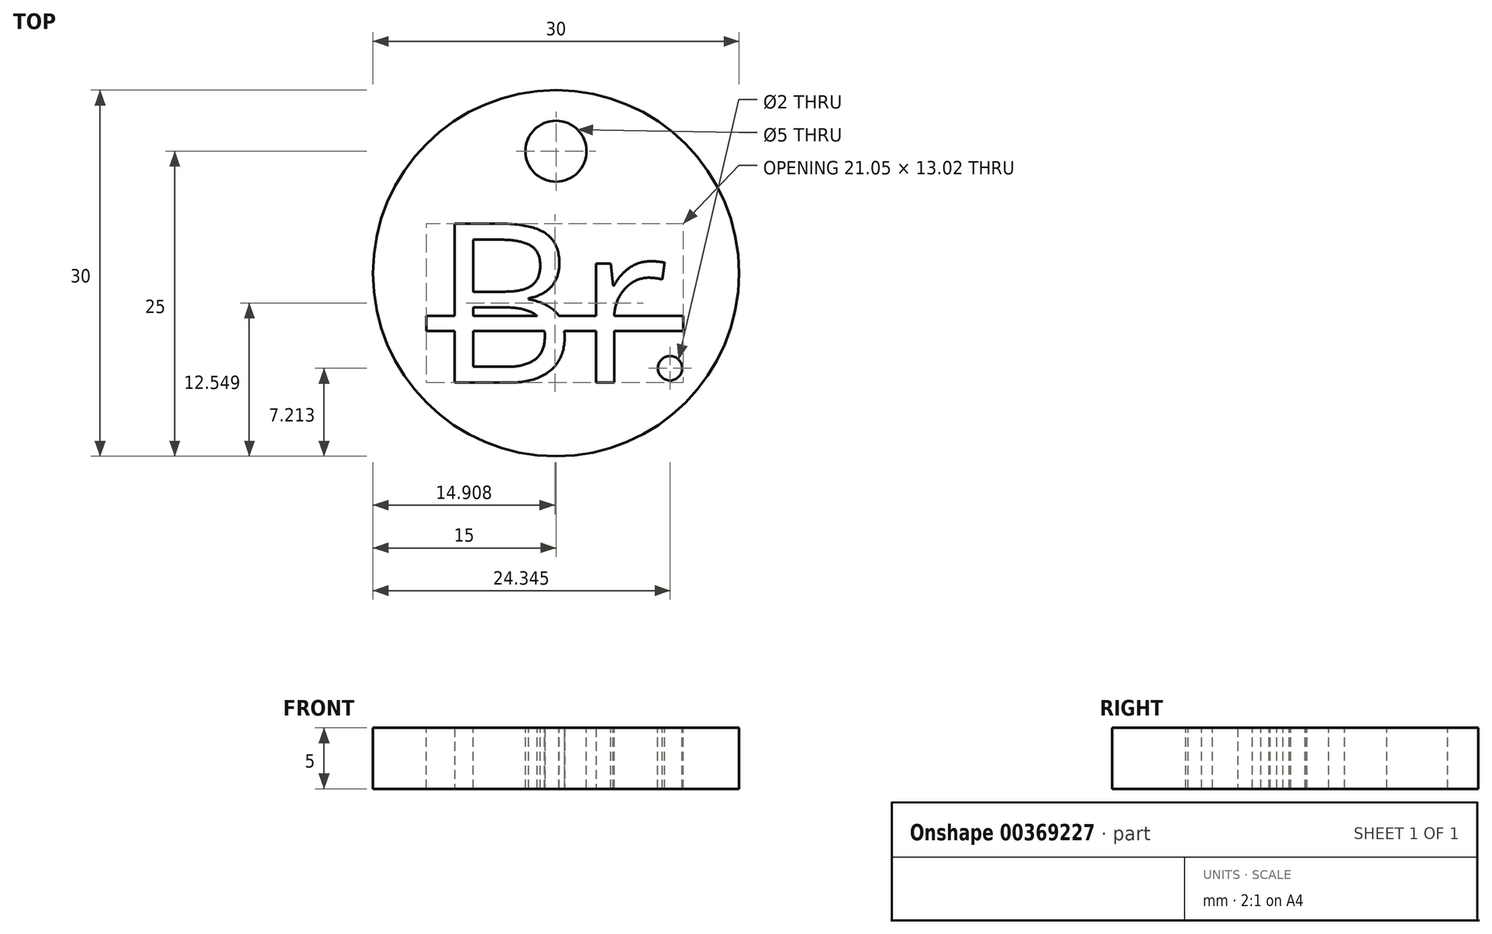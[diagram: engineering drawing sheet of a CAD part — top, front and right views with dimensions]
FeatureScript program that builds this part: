
annotation { "Feature Type Name" : "Feature", "Feature Type Description" : "" }
export const myFeature = defineFeature(function(context is Context, id is Id, definition is map)
    precondition{}
    {
        {
            var Q0;
            Q0=qCreatedBy(makeId("Top.planeOp"),FACE);
            var sketch = newSketch(context, id + "F0", { "sketchPlane" : qUnion([Q0])});
            skCircle(sketch, "E0", {"center": v(0, 0) * mm, "radius": 15 * mm});
            skSolve(sketch);
        }
        {
            var Q0;
            Q0=makeQuery(id+"F0.imprint","IMPRINT",FACE,{"disambiguationData":[TD([[makeQuery(id+"F0.imprint","IMPRINT",EDGE,{"derivedFrom":sQuery(id+"F0.wireOp",EDGE,"E0")}),1.0]])]});
            extrude(context, id + "F1", {"entities" : qUnion([Q0]), "depth" : 5 * mm});
        }
        {
            var Q0;
            Q0=makeQuery(id+"F1.opExtrude","CAP_FACE",FACE,{"disambiguationData":[OSD([sQuery(id+"F0.wireOp",EDGE,"E0")])],"isStart":false});
            var sketch = newSketch(context, id + "F2", { "sketchPlane" : qUnion([Q0])});
            skText(sketch, "E1", { "text": "Br", "fontName": "OpenSans-Regular.ttf"});
            const initialGuessF2  = {"E1": [-0.0101, -0.00896, 1, 0, 0.01313]};
            skSetInitialGuess(sketch, initialGuessF2);
            skSolve(sketch);
        }
        {
            var Q0;
            Q0 = qSketchRegion(id + "F2", true);
            extrude(context, id + "F3", {"entities" : qUnion([Q0]), "operationType" : NewBodyOperationType.REMOVE, "oppositeDirection" : true, "depth" : 25 * mm});
        }
        {
            var Q0;
            {var subQ0=sQuery(id+"F0.wireOp",EDGE,"E0");Q0=makeQuery(id+"F3.boolean.opBoolean","SPLIT",FACE,{"disambiguationData":[TD([makeQuery(id+"F1.opExtrude","SWEPT_FACE",FACE,{"disambiguationData":[OSD([subQ0])]})])],"derivedFrom":makeQuery(id+"F1.opExtrude","CAP_FACE",FACE,{"disambiguationData":[OSD([subQ0])],"isStart":false})});}
            var sketch = newSketch(context, id + "F4", { "sketchPlane" : qUnion([Q0])});
            skLineSegment(sketch, "E2.bottom", {"start": v(-10.61, -3.5) * mm, "end": v(10.43, -3.5) * mm});
            skLineSegment(sketch, "E2.top", {"start": v(-10.61, -4.72) * mm, "end": v(10.43, -4.72) * mm});
            skLineSegment(sketch, "E2.left", {"start": v(-10.61, -3.5) * mm, "end": v(-10.61, -4.72) * mm});
            skLineSegment(sketch, "E2.right", {"start": v(10.43, -3.5) * mm, "end": v(10.43, -4.72) * mm});
            skCircle(sketch, "E3", {"center": v(9.35, -7.79) * mm, "radius": 1 * mm});
            skSolve(sketch);
        }
        {
            var Q0;
            Q0 = qSketchRegion(id + "F4", true);
            extrude(context, id + "F5", {"entities" : qUnion([Q0]), "operationType" : NewBodyOperationType.REMOVE, "endBound" : BoundingType.THROUGH_ALL, "oppositeDirection" : true, "depth" : 25 * mm});
        }
        {
            var Q0;
            {var subQ0=sQuery(id+"F0.wireOp",EDGE,"E0");Q0=makeQuery(id+"F3.boolean.opBoolean","SPLIT",FACE,{"disambiguationData":[TD([makeQuery(id+"F1.opExtrude","SWEPT_FACE",FACE,{"disambiguationData":[OSD([subQ0])]})])],"derivedFrom":makeQuery(id+"F1.opExtrude","CAP_FACE",FACE,{"disambiguationData":[OSD([subQ0])],"isStart":false})});}
            var sketch = newSketch(context, id + "F6", { "sketchPlane" : qUnion([Q0])});
            skCircle(sketch, "E4", {"center": v(0, 10) * mm, "radius": 2.5 * mm});
            skSolve(sketch);
        }
        {
            var Q0;
            Q0 = qSketchRegion(id + "F6", true);
            extrude(context, id + "F7", {"entities" : qUnion([Q0]), "operationType" : NewBodyOperationType.REMOVE, "endBound" : BoundingType.UP_TO_NEXT, "oppositeDirection" : true, "depth" : 25 * mm});
        }
    });
